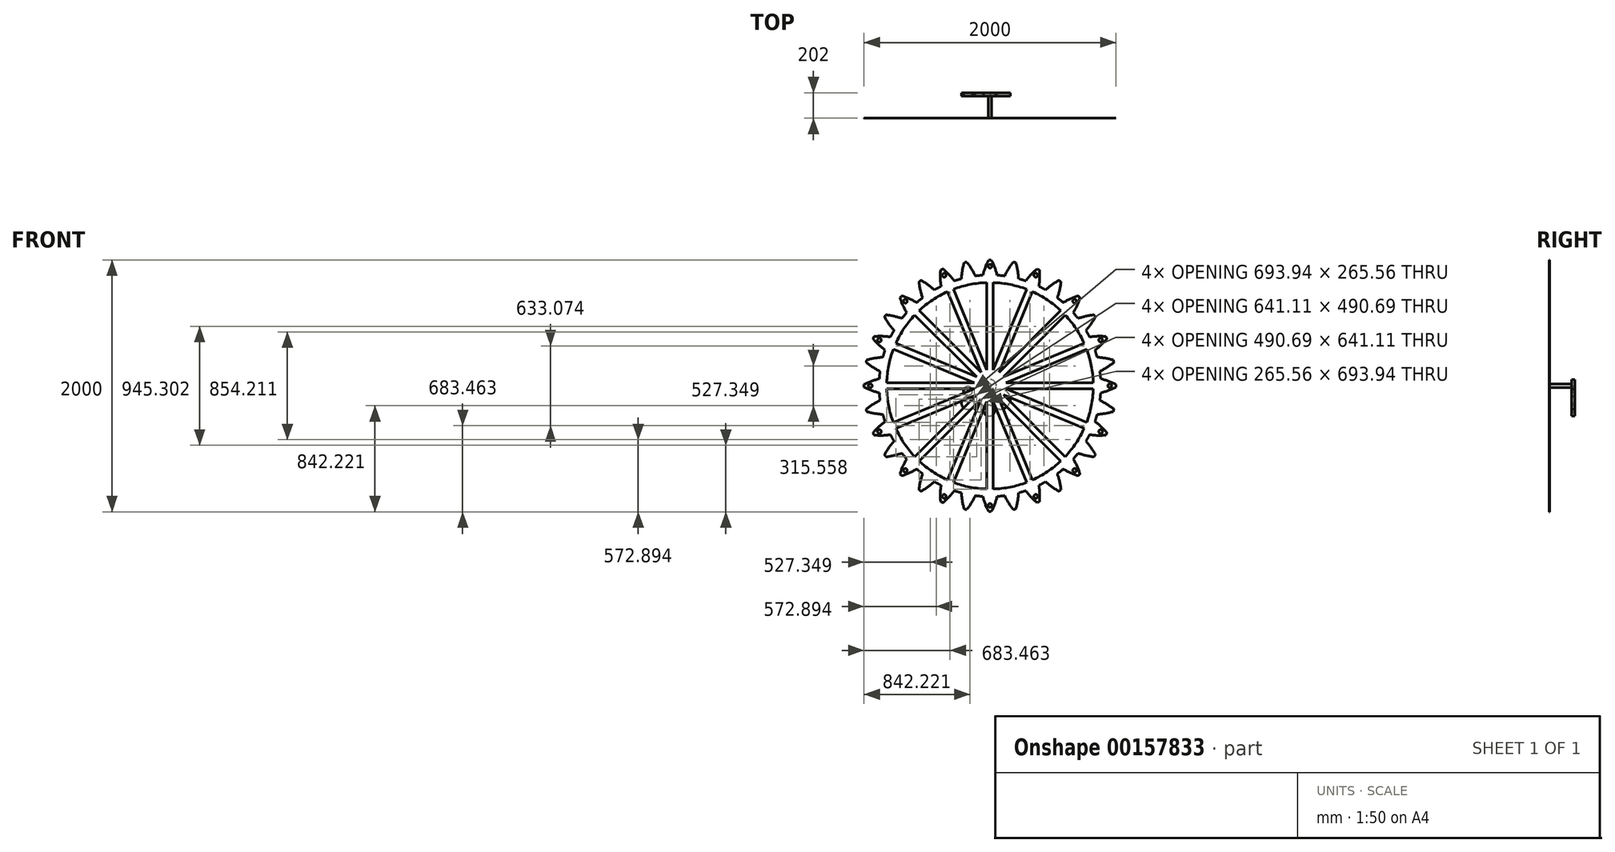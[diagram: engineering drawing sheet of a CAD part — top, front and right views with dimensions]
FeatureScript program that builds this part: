
annotation { "Feature Type Name" : "Feature", "Feature Type Description" : "" }
export const myFeature = defineFeature(function(context is Context, id is Id, definition is map)
    precondition{}
    {
        {
            var Q0;
            Q0=qCreatedBy(makeId("Front.planeOp"),FACE);
            var sketch = newSketch(context, id + "F0", { "sketchPlane" : qUnion([Q0])});
            skLineSegment(sketch, "E0.bottom", {"start": v(-250, 200) * mm, "end": v(250, 200) * mm});
            skLineSegment(sketch, "E0.top", {"start": v(-250, -400) * mm, "end": v(250, -400) * mm});
            skLineSegment(sketch, "E0.left", {"start": v(-250, 200) * mm, "end": v(-250, -400) * mm});
            skLineSegment(sketch, "E0.right", {"start": v(250, 200) * mm, "end": v(250, -400) * mm});
            skLineSegment(sketch, "E1.bottom", {"start": v(0, 0) * mm, "end": v(0, 0) * mm});
            skLineSegment(sketch, "E1.top", {"start": v(0, 200) * mm, "end": v(0, 200) * mm});
            skLineSegment(sketch, "E1.left", {"start": v(0, 0) * mm, "end": v(0, 200) * mm, "construction": true});
            skLineSegment(sketch, "E1.right", {"start": v(0, 0) * mm, "end": v(0, 200) * mm, "construction": true});
            skSolve(sketch);
        }
        {
            var Q0;
            Q0=makeQuery(id+"F0.imprint","IMPRINT",FACE,{"disambiguationData":[TD([[makeQuery(id+"F0.imprint","IMPRINT",EDGE,{"derivedFrom":sQuery(id+"F0.wireOp",EDGE,"E0.bottom")}),-1.0]])]});
            var sketch = newSketch(context, id + "F1", { "sketchPlane" : qUnion([Q0])});
            skCircle(sketch, "E2", {"center": v(0, 0) * mm, "radius": 50.36 * mm});
            skCircle(sketch, "E3", {"center": v(83, -106.57) * mm, "radius": 78.43 * mm});
            skCircle(sketch, "E4", {"center": v(-6.83, -197.56) * mm, "radius": 43.3 * mm});
            skCircle(sketch, "E5", {"center": v(-87.46, -172.22) * mm, "radius": 34.86 * mm});
            skCircle(sketch, "E6", {"center": v(-175, -136.51) * mm, "radius": 50.8 * mm});
            skCircle(sketch, "E7", {"center": v(-175, -40.91) * mm, "radius": 35.78 * mm});
            skCircle(sketch, "E8", {"center": v(0, 0) * mm, "radius": 13.23 * mm});
            skSolve(sketch);
        }
        {
            var Q0;
            Q0=makeQuery(id+"F1.imprint","IMPRINT",FACE,{"disambiguationData":[TD([[makeQuery(id+"F1.imprint","IMPRINT",EDGE,{"derivedFrom":sQuery(id+"F1.wireOp",EDGE,"E2")}),1.0]])]});
            var Q1;
            Q1=makeQuery(id+"F1.imprint","IMPRINT",FACE,{"disambiguationData":[TD([[makeQuery(id+"F1.imprint","IMPRINT",EDGE,{"derivedFrom":sQuery(id+"F1.wireOp",EDGE,"E3")}),1.0]])]});
            var Q2;
            Q2=makeQuery(id+"F1.imprint","IMPRINT",FACE,{"disambiguationData":[TD([[makeQuery(id+"F1.imprint","IMPRINT",EDGE,{"derivedFrom":sQuery(id+"F1.wireOp",EDGE,"E4")}),1.0]])]});
            var Q3;
            Q3=makeQuery(id+"F1.imprint","IMPRINT",FACE,{"disambiguationData":[TD([[makeQuery(id+"F1.imprint","IMPRINT",EDGE,{"derivedFrom":sQuery(id+"F1.wireOp",EDGE,"E5")}),1.0]])]});
            var Q4;
            Q4=makeQuery(id+"F1.imprint","IMPRINT",FACE,{"disambiguationData":[TD([[makeQuery(id+"F1.imprint","IMPRINT",EDGE,{"derivedFrom":sQuery(id+"F1.wireOp",EDGE,"E6")}),1.0]])]});
            var Q5;
            Q5=makeQuery(id+"F1.imprint","IMPRINT",FACE,{"disambiguationData":[TD([[makeQuery(id+"F1.imprint","IMPRINT",EDGE,{"derivedFrom":sQuery(id+"F1.wireOp",EDGE,"E7")}),1.0]])]});
            var Q6;
            Q6=sQuery(id+"F1.wireOp",EDGE,"E2");
            var Q7;
            Q7=sQuery(id+"F1.wireOp",EDGE,"E3");
            var Q8;
            Q8=sQuery(id+"F1.wireOp",EDGE,"E4");
            var Q9;
            Q9=sQuery(id+"F1.wireOp",EDGE,"E5");
            var Q10;
            Q10=sQuery(id+"F1.wireOp",EDGE,"E6");
            var Q11;
            Q11=sQuery(id+"F1.wireOp",EDGE,"E7");
            extrude(context, id + "F2", {"entities" : qUnion([Q0, Q1, Q2, Q3, Q4, Q5]), "surfaceEntities" : qUnion([Q6, Q7, Q8, Q9, Q10, Q11]), "depth" : 25 * mm});
        }
        {
            var Q0;
            Q0=makeQuery(id+"F1.imprint","IMPRINT",FACE,{"disambiguationData":[TD([[makeQuery(id+"F1.imprint","IMPRINT",EDGE,{"derivedFrom":sQuery(id+"F1.wireOp",EDGE,"E8")}),1.0]])]});
            extrude(context, id + "F3", {"entities" : qUnion([Q0]), "operationType" : NewBodyOperationType.ADD, "depth" : 200 * mm});
        }
        {
            var Q0;
            Q0=makeQuery(id+"F3.opExtrude","CAP_FACE",FACE,{"disambiguationData":[OSD([sQuery(id+"F1.wireOp",EDGE,"E8")])],"isStart":false});
            var sketch = newSketch(context, id + "F4", { "sketchPlane" : qUnion([Q0])});
            skCircle(sketch, "E9", {"center": v(0, 0) * mm, "radius": 1000 * mm, "construction": true});
            skLineSegment(sketch, "E10", {"start": v(0, 0) * mm, "end": v(1000, 0) * mm, "construction": true});
            skLineSegment(sketch, "E11", {"start": v(0, 0) * mm, "end": v(980.79, 195.1) * mm, "construction": true});
            skArc(sketch, "E12", {"start": v(1000, 0) * mm, "mid": v(999.99, 5) * mm, "end": v(999.95, 10) * mm});
            skArc(sketch, "E13", {"start": v(999.95, 10) * mm, "mid": v(940.5, 36.87) * mm, "end": v(878.2, 56.26) * mm});
            skArc(sketch, "E14", {"start": v(819.62, 25) * mm, "mid": v(814.73, 92.8) * mm, "end": v(804.24, 159.97) * mm});
            skLineSegment(sketch, "E15", {"start": v(819.62, 25) * mm, "end": v(125.68, 25) * mm});
            skLineSegment(sketch, "E16", {"start": v(125.68, 25) * mm, "end": v(0, 0) * mm});
            skLineSegment(sketch, "E17", {"start": v(0, 0) * mm, "end": v(995.18, 98.02) * mm, "construction": true});
            skArc(sketch, "E18", {"start": v(878.2, 56.26) * mm, "mid": v(877.1, 71.27) * mm, "end": v(875.76, 86.26) * mm});
            skArc(sketch, "E19.MirrorCS", {"start": v(980.79, 195.1) * mm, "mid": v(981.75, 190.18) * mm, "end": v(982.69, 185.27) * mm});
            skArc(sketch, "E20.MirrorCS", {"start": v(872.3, 116.15) * mm, "mid": v(874.16, 101.22) * mm, "end": v(875.76, 86.26) * mm});
            skArc(sketch, "E21.MirrorCS", {"start": v(982.69, 185.27) * mm, "mid": v(929.62, 147.32) * mm, "end": v(872.3, 116.15) * mm});
            skLineSegment(sketch, "E22", {"start": v(804.24, 159.97) * mm, "end": v(980.79, 195.1) * mm});
            skArc(sketch, "E23.MirrorCS", {"start": v(980.79, -195.1) * mm, "mid": v(981.75, -190.18) * mm, "end": v(982.69, -185.27) * mm});
            skArc(sketch, "E24.MirrorCS", {"start": v(878.2, -56.26) * mm, "mid": v(877.1, -71.27) * mm, "end": v(875.76, -86.26) * mm});
            skArc(sketch, "E25.MirrorCS", {"start": v(872.3, -116.15) * mm, "mid": v(874.16, -101.22) * mm, "end": v(875.76, -86.26) * mm});
            skArc(sketch, "E26.MirrorCS", {"start": v(1000, 0) * mm, "mid": v(999.99, -5) * mm, "end": v(999.95, -10) * mm});
            skLineSegment(sketch, "E27.MirrorCS", {"start": v(125.68, -25) * mm, "end": v(0, 0) * mm});
            skLineSegment(sketch, "E28.MirrorCS", {"start": v(819.62, -25) * mm, "end": v(125.68, -25) * mm});
            skLineSegment(sketch, "E29.MirrorCS", {"start": v(804.24, -159.97) * mm, "end": v(980.79, -195.1) * mm});
            skArc(sketch, "E30.MirrorCS", {"start": v(982.69, -185.27) * mm, "mid": v(929.62, -147.32) * mm, "end": v(872.3, -116.15) * mm});
            skArc(sketch, "E31.MirrorCS", {"start": v(819.62, -25) * mm, "mid": v(814.73, -92.8) * mm, "end": v(804.24, -159.97) * mm});
            skArc(sketch, "E32.MirrorCS", {"start": v(999.95, -10) * mm, "mid": v(940.5, -36.87) * mm, "end": v(878.2, -56.26) * mm});
            skCircle(sketch, "E33", {"center": v(950, 0) * mm, "radius": 15 * mm});
            skSolve(sketch);
        }
        {
            var Q0;
            {var subQ0=sQuery(id+"F4.wireOp",EDGE,"E27.MirrorCS");var subQ1=sQuery(id+"F4.wireOp",EDGE,"E16");var subQ2=makeQuery(id+"F4.imprint","INTERSECT",VERTEX,{"derivedFrom":[subQ1,subQ0]});Q0=makeQuery(id+"F4.imprint","IMPRINT",FACE,{"disambiguationData":[TD([[makeQuery(id+"F4.imprint","IMPRINT",EDGE,{"disambiguationData":[TD([[subQ2,1.0]])],"derivedFrom":subQ1}),1.0]])]});}
            var Q1;
            Q1=makeQuery(id+"F4.imprint","IMPRINT",FACE,{"disambiguationData":[TD([[makeQuery(id+"F4.imprint","IMPRINT",EDGE,{"derivedFrom":sQuery(id+"F4.wireOp",EDGE,"E12")}),1.0]])]});
            extrude(context, id + "F5", {"entities" : qUnion([Q0, Q1]), "depth" : 2 * mm});
        }
        {
            var Q0;
            Q0=makeQuery(id+"F5.opExtrude","SWEPT_BODY",BODY,{"disambiguationData":[OSD([sQuery(id+"F4.wireOp",EDGE,"E12"),sQuery(id+"F4.wireOp",EDGE,"E13"),sQuery(id+"F4.wireOp",EDGE,"E14"),sQuery(id+"F4.wireOp",EDGE,"E15"),sQuery(id+"F4.wireOp",EDGE,"E16"),sQuery(id+"F4.wireOp",EDGE,"E18"),sQuery(id+"F4.wireOp",EDGE,"E19.MirrorCS"),sQuery(id+"F4.wireOp",EDGE,"E20.MirrorCS"),sQuery(id+"F4.wireOp",EDGE,"E21.MirrorCS"),sQuery(id+"F4.wireOp",EDGE,"E22"),sQuery(id+"F4.wireOp",EDGE,"E23.MirrorCS"),sQuery(id+"F4.wireOp",EDGE,"E24.MirrorCS"),sQuery(id+"F4.wireOp",EDGE,"E25.MirrorCS"),sQuery(id+"F4.wireOp",EDGE,"E26.MirrorCS"),sQuery(id+"F4.wireOp",EDGE,"E27.MirrorCS"),sQuery(id+"F4.wireOp",EDGE,"E28.MirrorCS"),sQuery(id+"F4.wireOp",EDGE,"E29.MirrorCS"),sQuery(id+"F4.wireOp",EDGE,"E30.MirrorCS"),sQuery(id+"F4.wireOp",EDGE,"E31.MirrorCS"),sQuery(id+"F4.wireOp",EDGE,"E32.MirrorCS")])]});
            var Q1;
            Q1=sQuery(id+"F1.wireOp",EDGE,"E2");
            circularPattern(context, id + "F6", {"operationType" : NewBodyOperationType.ADD, "entities" : qUnion([Q0]), "axis" : qUnion([Q1]), "angle" : 360 * degree, "instanceCount" : 16, "equalSpace" : true});
        }
    });
